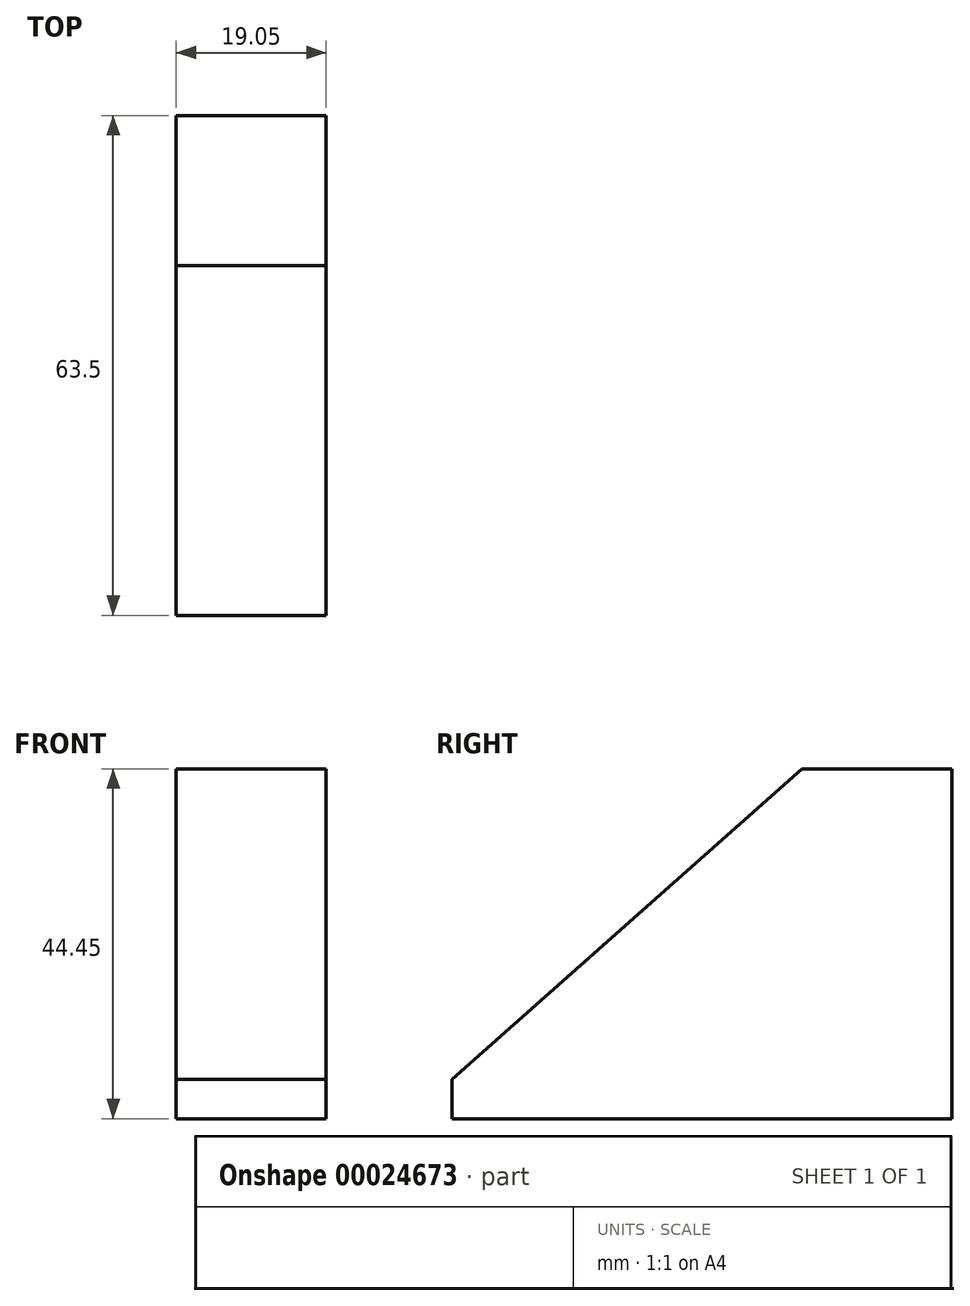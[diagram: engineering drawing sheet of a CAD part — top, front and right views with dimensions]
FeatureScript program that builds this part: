
annotation { "Feature Type Name" : "Feature", "Feature Type Description" : "" }
export const myFeature = defineFeature(function(context is Context, id is Id, definition is map)
    precondition{}
    {
        {
            var Q0;
            Q0=qCreatedBy(makeId("Right.planeOp"),FACE);
            var sketch = newSketch(context, id + "F0", { "sketchPlane" : qUnion([Q0])});
            skLineSegment(sketch, "E0", {"start": v(-82.15, 32.2) * mm, "end": v(-82.15, -12.26) * mm});
            skLineSegment(sketch, "E1.MirrorCS", {"start": v(-82.15, 32.2) * mm, "end": v(-101.2, 32.2) * mm});
            skLineSegment(sketch, "E2.MirrorCS", {"start": v(-101.2, 32.2) * mm, "end": v(-145.65, -7.25) * mm});
            skLineSegment(sketch, "E3.MirrorCS", {"start": v(-145.65, -12.26) * mm, "end": v(-145.65, -7.25) * mm});
            skLineSegment(sketch, "E4.MirrorCS", {"start": v(-82.15, -12.26) * mm, "end": v(-145.65, -12.26) * mm});
            skPoint(sketch, "E5.start.orphan", {"position": v(-63.1, 32.2) * mm});
            skPoint(sketch, "E6.end.orphan", {"position": v(-18.65, -7.25) * mm});
            skPoint(sketch, "E6.start.orphan", {"position": v(-18.65, -12.26) * mm});
            skSolve(sketch);
        }
        {
            var Q0;
            Q0 = qSketchRegion(id + "F0", true);
            extrude(context, id + "F1", {"entities" : qUnion([Q0]), "depth" : 19.05 * mm});
        }
    });
